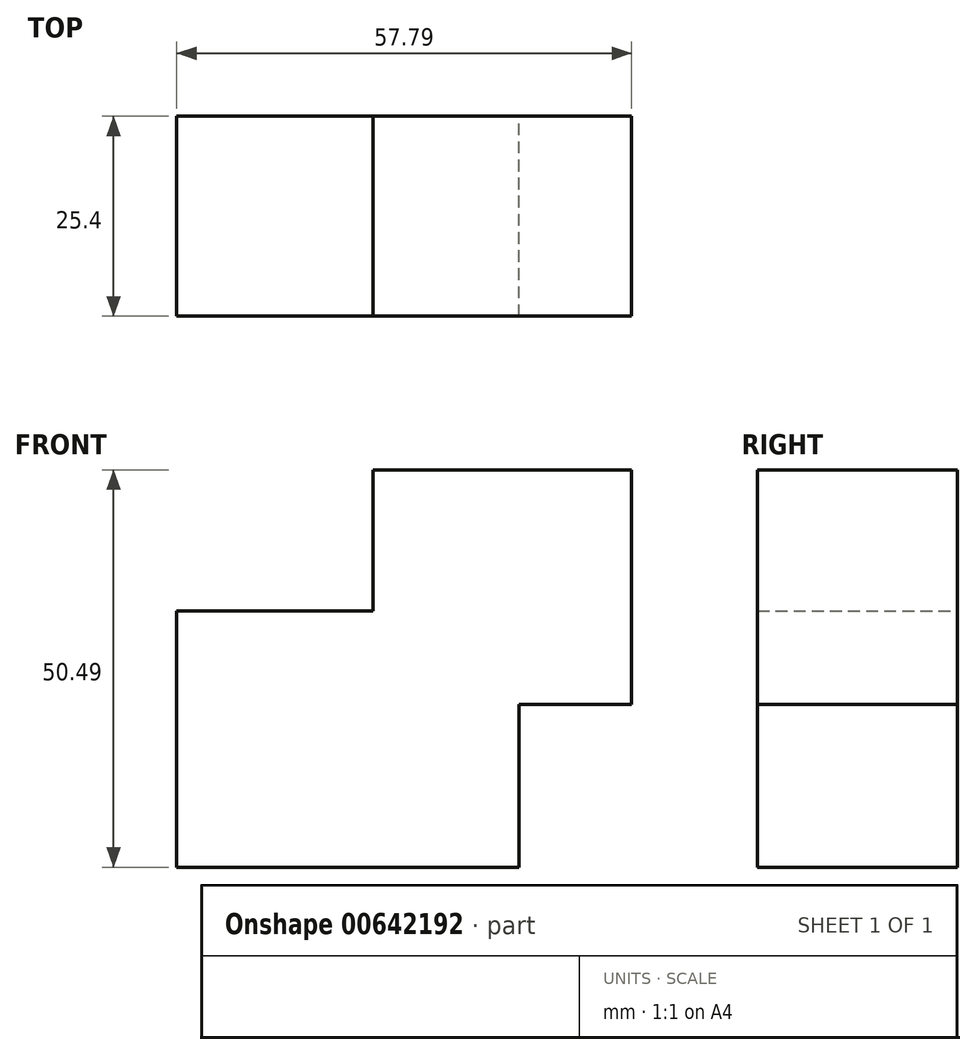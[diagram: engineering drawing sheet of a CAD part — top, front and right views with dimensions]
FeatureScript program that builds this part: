
annotation { "Feature Type Name" : "Feature", "Feature Type Description" : "" }
export const myFeature = defineFeature(function(context is Context, id is Id, definition is map)
    precondition{}
    {
        {
            var Q0;
            Q0=qCreatedBy(makeId("Front.planeOp"),FACE);
            var sketch = newSketch(context, id + "F0", { "sketchPlane" : qUnion([Q0])});
            skLineSegment(sketch, "E0.bottom", {"start": v(-2.59, 35.28) * mm, "end": v(22.35, 35.28) * mm});
            skLineSegment(sketch, "E0.top", {"start": v(-2.59, 2.74) * mm, "end": v(40.9, 2.74) * mm});
            skLineSegment(sketch, "E0.left", {"start": v(-2.59, 35.28) * mm, "end": v(-2.59, 2.74) * mm});
            skLineSegment(sketch, "E0.right", {"start": v(40.9, 23.42) * mm, "end": v(40.9, 2.74) * mm});
            skLineSegment(sketch, "E1.bottom", {"start": v(22.35, 53.23) * mm, "end": v(55.2, 53.23) * mm});
            skLineSegment(sketch, "E1.top", {"start": v(40.9, 23.42) * mm, "end": v(55.2, 23.42) * mm});
            skLineSegment(sketch, "E1.left", {"start": v(22.35, 53.23) * mm, "end": v(22.35, 35.28) * mm});
            skLineSegment(sketch, "E1.right", {"start": v(55.2, 53.23) * mm, "end": v(55.2, 23.42) * mm});
            skSolve(sketch);
        }
        {
            var Q0;
            Q0 = qSketchRegion(id + "F0", true);
            extrude(context, id + "F1", {"entities" : qUnion([Q0]), "depth" : 25.4 * mm, "offsetDistance" : 25.4 * mm});
        }
    });
